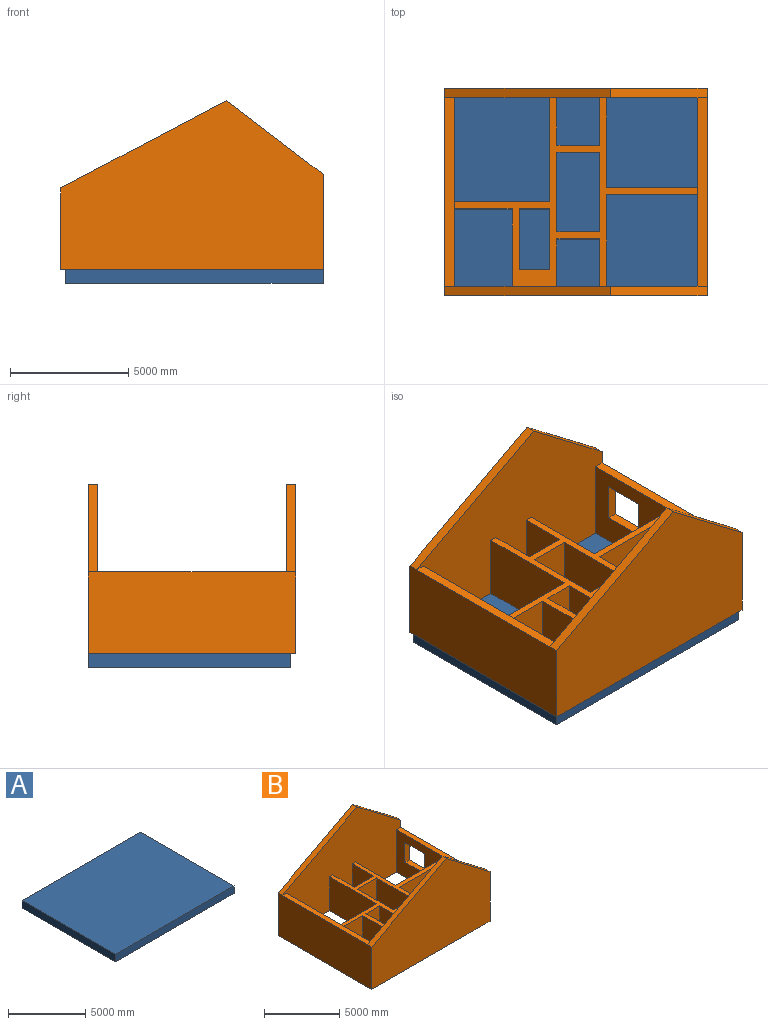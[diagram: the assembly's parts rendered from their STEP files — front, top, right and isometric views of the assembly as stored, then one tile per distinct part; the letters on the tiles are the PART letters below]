
ASSEMBLY  parts=2 mates=1
PART A: 6 faces, bbox 10890x8570x600 mm
  f0: plane 8570x600mm, normal (-1,0,0), area 5142000mm2, adj f1,f3,f4,f5
  f1: plane 10890x600mm, normal (0,-1,0), area 6534000mm2, adj f0,f2,f4,f5
  f2: plane 8570x600mm, normal (1,0,0), area 5142000mm2, adj f1,f3,f4,f5
  f3: plane 10890x600mm, normal (0,1,0), area 6534000mm2, adj f0,f2,f4,f5
  f4: plane 10890x8570mm, normal (0,0,1), area 93327300mm2, adj f0,f1,f2,f3
  f5: plane 10890x8570mm, normal (0,0,-1), area 93327300mm2, adj f0,f1,f2,f3
PART B: 46 faces, bbox 11090x8770x7140 mm
  f0: plane 7970x400mm, normal (0,0,1), area 3188000mm2, adj f2,f4,f5,f9
  f1: plane 7970x400mm, normal (0,0,1), area 3188000mm2, adj f2,f3,f7,f9
  f2: plane 11090x7140mm, normal (0,-1,0), area 55453100mm2, adj f0,f1,f3,f4,f7,f10,f11,f13
  f3: plane 7970x3440mm, normal (-1,0,0), area 20831800mm2, adj f1,f2,f9,f10,f22,f23,f33,f38
  f4: plane 7970x3440mm, normal (1,0,0), area 26591800mm2, adj f0,f2,f9,f10,f15,f16,f33
  f5: plane 8770x3440mm, normal (-1,0,0), area 30168800mm2, adj f0,f6,f8,f10,f35,f36
  f6: plane 11090x7140mm, normal (0,-1,0), area 59855100mm2, adj f5,f7,f10,f34,f35
  f7: plane 8770x4020mm, normal (1,0,0), area 24872800mm2, adj f1,f2,f6,f8,f9,f10,f34,f37
  f8: plane 11090x7140mm, normal (0,1,0), area 59855100mm2, adj f5,f7,f10,f36,f37
  f9: plane 11090x7140mm, normal (0,1,0), area 51053100mm2, adj f0,f1,f3,f4,f7,f10,f17,f18
  f10: plane 11090x8770mm, normal (0,0,-1), area 25381000mm2, adj f2,f3,f4,f5,f6,f7,f8,f9
  f11: plane 2750x2000mm, normal (-1,0,0), area 5500000mm2, adj f2,f10,f12,f33
  f12: plane 2750x1800mm, normal (0,1,0), area 4950000mm2, adj f10,f11,f13,f33
  f13: plane 2750x2000mm, normal (1,0,0), area 5500000mm2, adj f2,f10,f12,f33
  f14: plane 4400x2750mm, normal (-1,0,0), area 12100000mm2, adj f2,f10,f15,f33
  f15: plane 4040x2750mm, normal (0,1,0), area 11110000mm2, adj f4,f10,f14,f33
  f16: plane 2750x2440mm, normal (0,-1,0), area 6710000mm2, adj f4,f10,f17,f33
  f17: plane 3270x2750mm, normal (-1,0,0), area 8992500mm2, adj f9,f10,f16,f33
  f18: plane 2750x2000mm, normal (1,0,0), area 5500000mm2, adj f9,f10,f19,f33
  f19: plane 2750x1800mm, normal (0,-1,0), area 4950000mm2, adj f10,f18,f20,f33
  f20: plane 2750x2000mm, normal (-1,0,0), area 5500000mm2, adj f9,f10,f19,f33
  f21: plane 3870x2750mm, normal (1,0,0), area 10642500mm2, adj f9,f10,f22,f33
  f22: plane 3850x2750mm, normal (0,-1,0), area 10587500mm2, adj f3,f10,f21,f33
  f23: plane 3850x2750mm, normal (0,1,0), area 10587500mm2, adj f3,f10,f32,f33
  f24: plane 2750x2560mm, normal (1,0,0), area 7040000mm2, adj f10,f25,f30,f33
  f25: plane 2750x1300mm, normal (0,-1,0), area 3575000mm2, adj f10,f24,f26,f33
  f26: plane 2750x2560mm, normal (-1,0,0), area 7040000mm2, adj f10,f25,f30,f33
  f27: plane 3370x2750mm, normal (1,0,0), area 9267500mm2, adj f10,f28,f31,f33
  f28: plane 2750x1800mm, normal (0,-1,0), area 4950000mm2, adj f10,f27,f29,f33
  f29: plane 3370x2750mm, normal (-1,0,0), area 9267500mm2, adj f10,f28,f31,f33
  f30: plane 2750x1300mm, normal (0,1,0), area 3575000mm2, adj f10,f24,f26,f33
  f31: plane 2750x1800mm, normal (0,1,0), area 4950000mm2, adj f10,f27,f29,f33
  f32: plane 3800x2750mm, normal (1,0,0), area 10450000mm2, adj f2,f10,f23,f33
  f33: plane 10290x7970mm, normal (0,0,1), area 10133000mm2, adj f2,f3,f4,f9,f11,f12,f13,f14
  f34: plane 4100x3120mm, normal (0.61,0,0.8), area 2060850.3mm2, adj f6,f7,f9,f35
  f35: plane 6990x3700mm, normal (-0.47,0,0.88), area 3163544.8mm2, adj f5,f6,f9,f34
  f36: plane 6990x3700mm, normal (-0.47,0,0.88), area 3163544.8mm2, adj f2,f5,f8,f37
  f37: plane 4100x3120mm, normal (0.61,0,0.8), area 2060850.3mm2, adj f2,f7,f8,f36
  f38: plane 1600x400mm, normal (0,1,0), area 640000mm2, adj f3,f7,f39,f40
  f39: plane 1800x400mm, normal (0,0,-1), area 720000mm2, adj f3,f7,f38,f41
  f40: plane 1800x400mm, normal (0,0,1), area 720000mm2, adj f3,f7,f38,f41
  f41: plane 1600x400mm, normal (0,-1,0), area 640000mm2, adj f3,f7,f39,f40
  f42: plane 1600x400mm, normal (0,1,0), area 640000mm2, adj f3,f7,f43,f44
  f43: plane 1800x400mm, normal (0,0,-1), area 720000mm2, adj f3,f7,f42,f45
  f44: plane 1800x400mm, normal (0,0,1), area 720000mm2, adj f3,f7,f42,f45
  f45: plane 1600x400mm, normal (0,-1,0), area 640000mm2, adj f3,f7,f43,f44
PLACE A at identity fixed
PLACE B t=(-100,-100,0)mm
MATE fastened B.f10 <-> A.f4  axis (0,0,1) through (-200,-200,600)mm
